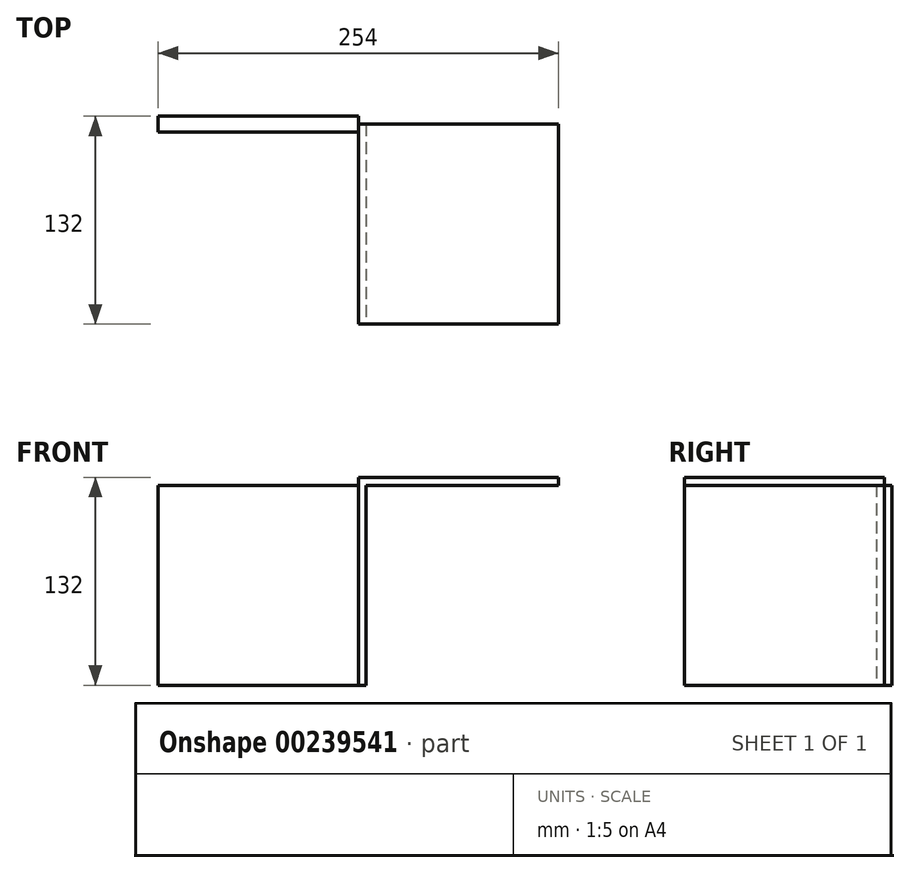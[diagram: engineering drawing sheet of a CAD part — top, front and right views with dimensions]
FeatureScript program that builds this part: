
annotation { "Feature Type Name" : "Feature", "Feature Type Description" : "" }
export const myFeature = defineFeature(function(context is Context, id is Id, definition is map)
    precondition{}
    {
        {
            assignVariable(context, id + "F0", {"name" : "L", "anyValue" : 5});
        }
        {
            var Q0;
            Q0=qCreatedBy(makeId("Front.planeOp"),FACE);
            var sketch = newSketch(context, id + "F1", { "sketchPlane" : qUnion([Q0])});
            skLineSegment(sketch, "E0.bottom", {"start": v(63.5, 63.5) * mm, "end": v(-63.5, 63.5) * mm});
            skLineSegment(sketch, "E0.top", {"start": v(63.5, -63.5) * mm, "end": v(-63.5, -63.5) * mm});
            skLineSegment(sketch, "E0.left", {"start": v(63.5, 63.5) * mm, "end": v(63.5, -63.5) * mm});
            skLineSegment(sketch, "E0.right", {"start": v(-63.5, 63.5) * mm, "end": v(-63.5, -63.5) * mm});
            skPoint(sketch, "E0.middle", {"position": v(0, 0) * mm});
            skSolve(sketch);
        }
        {
            var Q0;
            Q0 = qSketchRegion(id + "F1", true);
            extrude(context, id + "F2", {"entities" : qUnion([Q0]), "endBound" : BoundingType.SYMMETRIC, "depth" : (getVariable(context, 'L') * 2) * mm});
        }
        {
            var Q0;
            Q0=makeQuery(id+"F2.opExtrude","SWEPT_FACE",FACE,{"disambiguationData":[OSD([sQuery(id+"F1.wireOp",EDGE,"E0.left")])]});
            var sketch = newSketch(context, id + "F3", { "sketchPlane" : qUnion([Q0])});
            skLineSegment(sketch, "E1.bottom", {"start": v(0, 63.5) * mm, "end": v(-127, 63.5) * mm});
            skLineSegment(sketch, "E1.top", {"start": v(0, -63.5) * mm, "end": v(-127, -63.5) * mm});
            skLineSegment(sketch, "E1.left", {"start": v(0, 63.5) * mm, "end": v(0, -63.5) * mm});
            skLineSegment(sketch, "E1.right", {"start": v(-127, 63.5) * mm, "end": v(-127, -63.5) * mm});
            skSolve(sketch);
        }
        {
            var Q0;
            Q0 = qSketchRegion(id + "F3", true);
            extrude(context, id + "F4", {"entities" : qUnion([Q0]), "operationType" : NewBodyOperationType.ADD, "depth" : (getVariable(context, 'L')) * mm});
        }
        {
            var Q0;
            Q0=makeQuery(id+"F4.boolean.opBoolean","MERGE",FACE,{"derivedFrom":[makeQuery(id+"F2.opExtrude","SWEPT_FACE",FACE,{"disambiguationData":[OSD([sQuery(id+"F1.wireOp",EDGE,"E0.bottom")])]}),makeQuery(id+"F4.opExtrude","SWEPT_FACE",FACE,{"disambiguationData":[OSD([sQuery(id+"F3.wireOp",EDGE,"E1.bottom")])]})]});
            var sketch = newSketch(context, id + "F5", { "sketchPlane" : qUnion([Q0])});
            skLineSegment(sketch, "E2.bottom", {"start": v(63.5, 0) * mm, "end": v(190.5, 0) * mm});
            skLineSegment(sketch, "E2.top", {"start": v(63.5, -127) * mm, "end": v(190.5, -127) * mm});
            skLineSegment(sketch, "E2.left", {"start": v(63.5, 0) * mm, "end": v(63.5, -127) * mm});
            skLineSegment(sketch, "E2.right", {"start": v(190.5, 0) * mm, "end": v(190.5, -127) * mm});
            skSolve(sketch);
        }
        {
            var Q0;
            Q0 = qSketchRegion(id + "F5", true);
            extrude(context, id + "F6", {"entities" : qUnion([Q0]), "operationType" : NewBodyOperationType.ADD, "depth" : (getVariable(context, 'L')) * mm});
        }
    });
